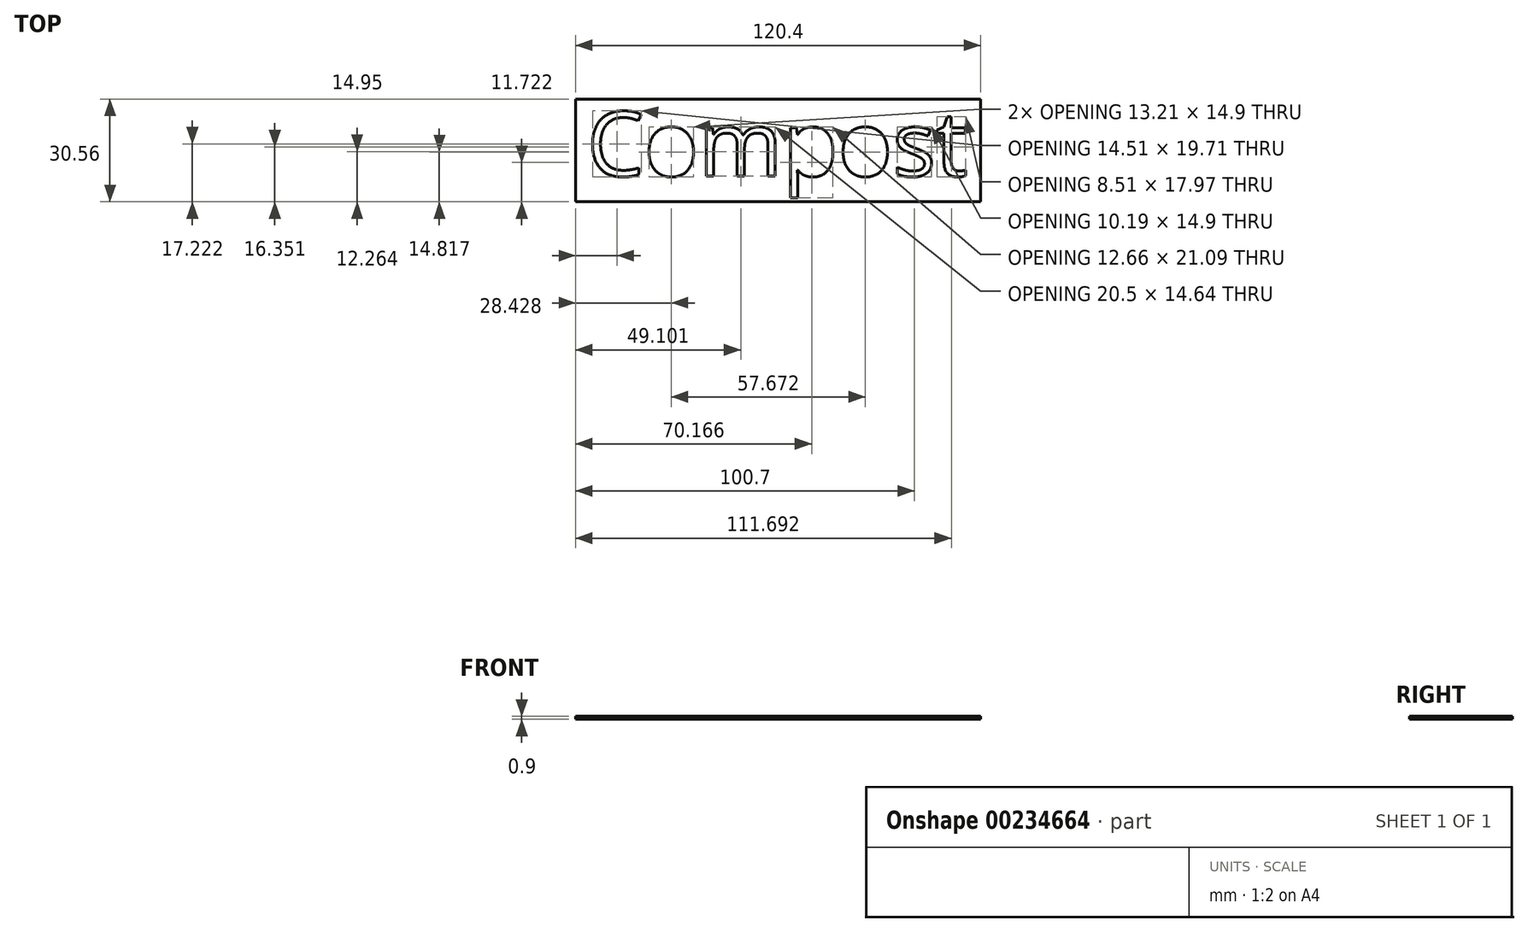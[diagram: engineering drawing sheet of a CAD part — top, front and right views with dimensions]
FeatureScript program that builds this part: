
annotation { "Feature Type Name" : "Feature", "Feature Type Description" : "" }
export const myFeature = defineFeature(function(context is Context, id is Id, definition is map)
    precondition{}
    {
        {
            var Q0;
            Q0=qCreatedBy(makeId("Top.planeOp"),FACE);
            var sketch = newSketch(context, id + "F0", { "sketchPlane" : qUnion([Q0])});
            skLineSegment(sketch, "E0.bottom", {"start": v(-62.37, 13.11) * mm, "end": v(58.03, 13.11) * mm});
            skLineSegment(sketch, "E0.top", {"start": v(-62.37, -17.45) * mm, "end": v(58.03, -17.45) * mm});
            skLineSegment(sketch, "E0.left", {"start": v(-62.37, 13.11) * mm, "end": v(-62.37, -17.45) * mm});
            skLineSegment(sketch, "E0.right", {"start": v(58.03, 13.11) * mm, "end": v(58.03, -17.45) * mm});
            skText(sketch, "E1", { "text": "Compost", "fontName": "OpenSans-Regular.ttf"});
            const initialGuessF0  = {"E1": [-0.059, -0.00982, 1, 0, 0.01934]};
            skSetInitialGuess(sketch, initialGuessF0);
            skSolve(sketch);
        }
        {
            var Q0;
            Q0 = qSketchRegion(id + "F0", true);
            extrude(context, id + "F1", {"entities" : qUnion([Q0]), "depth" : .9 * mm});
        }
    });
